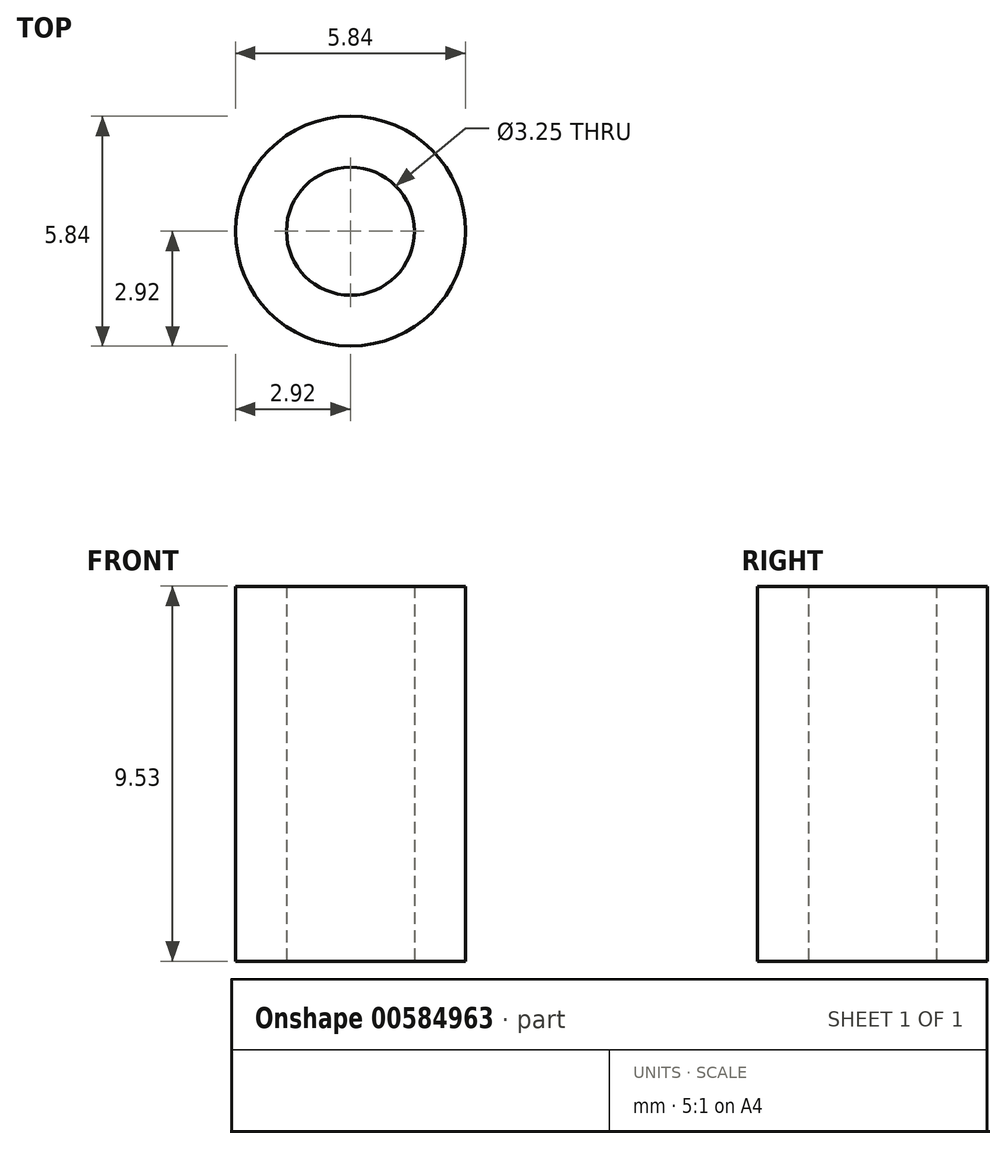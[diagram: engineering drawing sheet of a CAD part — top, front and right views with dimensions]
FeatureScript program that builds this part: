
annotation { "Feature Type Name" : "Feature", "Feature Type Description" : "" }
export const myFeature = defineFeature(function(context is Context, id is Id, definition is map)
    precondition{}
    {
        {
            var Q0;
            Q0=qCreatedBy(makeId("Top.planeOp"),FACE);
            var sketch = newSketch(context, id + "F0", { "sketchPlane" : qUnion([Q0])});
            skCircle(sketch, "E0", {"center": v(0, 0) * mm, "radius": 1.63 * mm});
            skCircle(sketch, "E1", {"center": v(0, 0) * mm, "radius": 2.92 * mm});
            skSolve(sketch);
        }
        {
            var Q0;
            Q0=makeQuery(id+"F0.imprint","IMPRINT",FACE,{"disambiguationData":[TD([[makeQuery(id+"F0.imprint","IMPRINT",EDGE,{"derivedFrom":sQuery(id+"F0.wireOp",EDGE,"E0")}),-1.0]])]});
            extrude(context, id + "F1", {"entities" : qUnion([Q0]), "depth" : 9.52 * mm, "offsetDistance" : 25.4 * mm});
        }
    });
